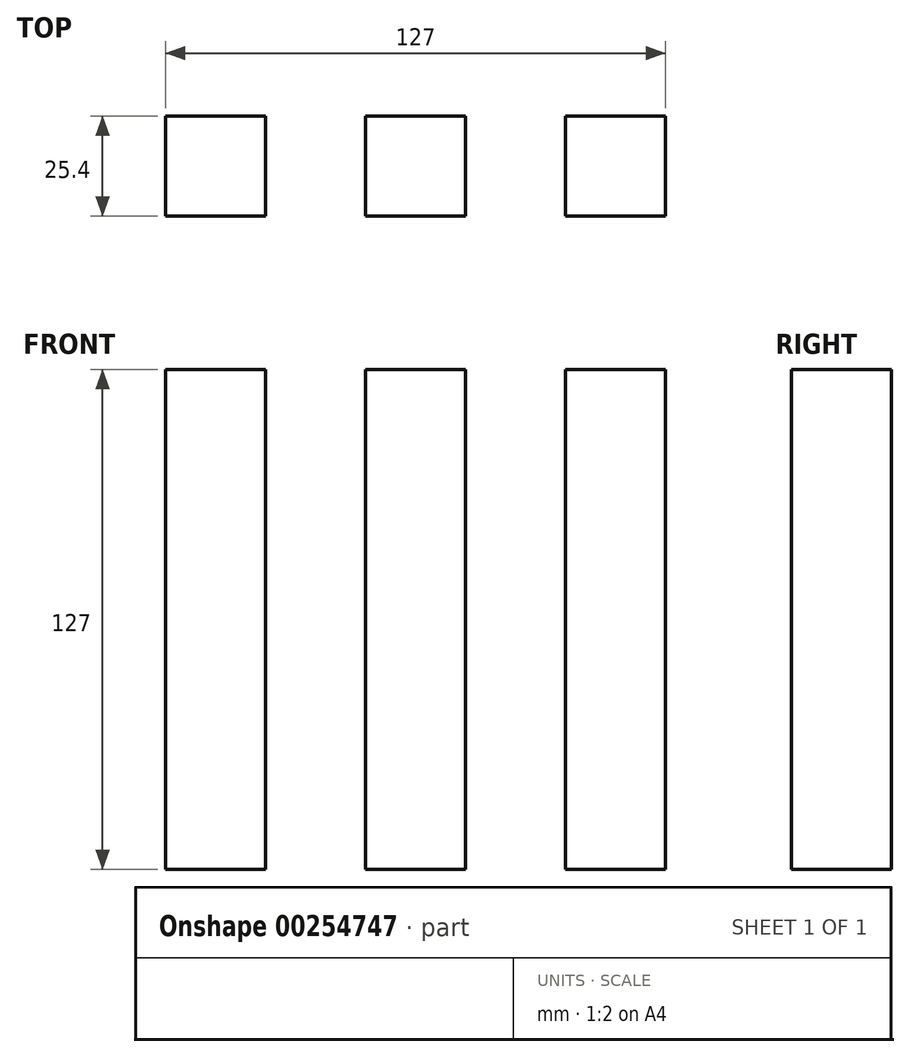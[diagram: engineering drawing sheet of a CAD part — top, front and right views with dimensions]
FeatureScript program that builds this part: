
annotation { "Feature Type Name" : "Feature", "Feature Type Description" : "" }
export const myFeature = defineFeature(function(context is Context, id is Id, definition is map)
    precondition{}
    {
        {
            var Q0;
            Q0=qCreatedBy(makeId("Front.planeOp"),FACE);
            var sketch = newSketch(context, id + "F0", { "sketchPlane" : qUnion([Q0])});
            skLineSegment(sketch, "E0", {"start": v(0, 0) * mm, "end": v(0, 76.2) * mm});
            skLineSegment(sketch, "E1.bottom", {"start": v(-12.7, 12.7) * mm, "end": v(12.7, 12.7) * mm});
            skLineSegment(sketch, "E1.top", {"start": v(-12.7, 139.7) * mm, "end": v(12.7, 139.7) * mm});
            skLineSegment(sketch, "E1.left", {"start": v(-12.7, 12.7) * mm, "end": v(-12.7, 139.7) * mm});
            skLineSegment(sketch, "E1.right", {"start": v(12.7, 12.7) * mm, "end": v(12.7, 139.7) * mm});
            skPoint(sketch, "E1.middle", {"position": v(0, 76.2) * mm});
            skLineSegment(sketch, "E2", {"start": v(0, 76.2) * mm, "end": v(-50.8, 76.2) * mm});
            skPoint(sketch, "E2.endSnap0", {"position": v(-12.7, 76.2) * mm});
            skLineSegment(sketch, "E3", {"start": v(0, 76.2) * mm, "end": v(50.8, 76.2) * mm});
            skLineSegment(sketch, "E4.bottom", {"start": v(-63.5, 12.7) * mm, "end": v(-38.1, 12.7) * mm});
            skLineSegment(sketch, "E4.top", {"start": v(-63.5, 139.7) * mm, "end": v(-38.1, 139.7) * mm});
            skLineSegment(sketch, "E4.left", {"start": v(-63.5, 12.7) * mm, "end": v(-63.5, 139.7) * mm});
            skLineSegment(sketch, "E4.right", {"start": v(-38.1, 12.7) * mm, "end": v(-38.1, 139.7) * mm});
            skPoint(sketch, "E4.middle", {"position": v(-50.8, 76.2) * mm});
            skLineSegment(sketch, "E5.bottom", {"start": v(38.1, 12.7) * mm, "end": v(63.5, 12.7) * mm});
            skLineSegment(sketch, "E5.top", {"start": v(38.1, 139.7) * mm, "end": v(63.5, 139.7) * mm});
            skLineSegment(sketch, "E5.left", {"start": v(38.1, 12.7) * mm, "end": v(38.1, 139.7) * mm});
            skLineSegment(sketch, "E5.right", {"start": v(63.5, 12.7) * mm, "end": v(63.5, 139.7) * mm});
            skPoint(sketch, "E5.middle", {"position": v(50.8, 76.2) * mm});
            skSolve(sketch);
        }
        {
            var Q0;
            {var subQ1=sQuery(id+"F0.wireOp",EDGE,"E4.bottom");Q0=makeQuery(id+"F0.imprint","IMPRINT",FACE,{"disambiguationData":[TD([[makeQuery(id+"F0.imprint","IMPRINT",EDGE,{"derivedFrom":subQ1}),1.0]])]});}
            var Q1;
            {var subQ6=sQuery(id+"F0.wireOp",EDGE,"E1.top");Q1=makeQuery(id+"F0.imprint","IMPRINT",FACE,{"disambiguationData":[TD([[makeQuery(id+"F0.imprint","IMPRINT",EDGE,{"derivedFrom":subQ6}),-1.0]])]});}
            var Q2;
            {var subQ3=sQuery(id+"F0.wireOp",EDGE,"E1.bottom");var subQ5=sQuery(id+"F0.wireOp",EDGE,"E1.right");var subQ6=makeQuery(id+"F0.imprint","INTERSECT",VERTEX,{"derivedFrom":[subQ3,subQ5]});Q2=makeQuery(id+"F0.imprint","IMPRINT",FACE,{"disambiguationData":[TD([[makeQuery(id+"F0.imprint","IMPRINT",EDGE,{"disambiguationData":[TD([[subQ6,1.0]])],"derivedFrom":subQ3}),1.0]])]});}
            var Q3;
            {var subQ3=sQuery(id+"F0.wireOp",EDGE,"E1.bottom");var subQ5=sQuery(id+"F0.wireOp",EDGE,"E1.left");var subQ6=makeQuery(id+"F0.imprint","INTERSECT",VERTEX,{"derivedFrom":[subQ3,subQ5]});Q3=makeQuery(id+"F0.imprint","IMPRINT",FACE,{"disambiguationData":[TD([[makeQuery(id+"F0.imprint","IMPRINT",EDGE,{"disambiguationData":[TD([[subQ6,-1.0]])],"derivedFrom":subQ3}),1.0]])]});}
            var Q4;
            {var subQ3=sQuery(id+"F0.wireOp",EDGE,"E5.bottom");Q4=makeQuery(id+"F0.imprint","IMPRINT",FACE,{"disambiguationData":[TD([[makeQuery(id+"F0.imprint","IMPRINT",EDGE,{"derivedFrom":subQ3}),1.0]])]});}
            extrude(context, id + "F1", {"entities" : qUnion([Q0, Q1, Q2, Q3, Q4]), "endBound" : BoundingType.SYMMETRIC, "depth" : 25.4 * mm});
        }
    });
